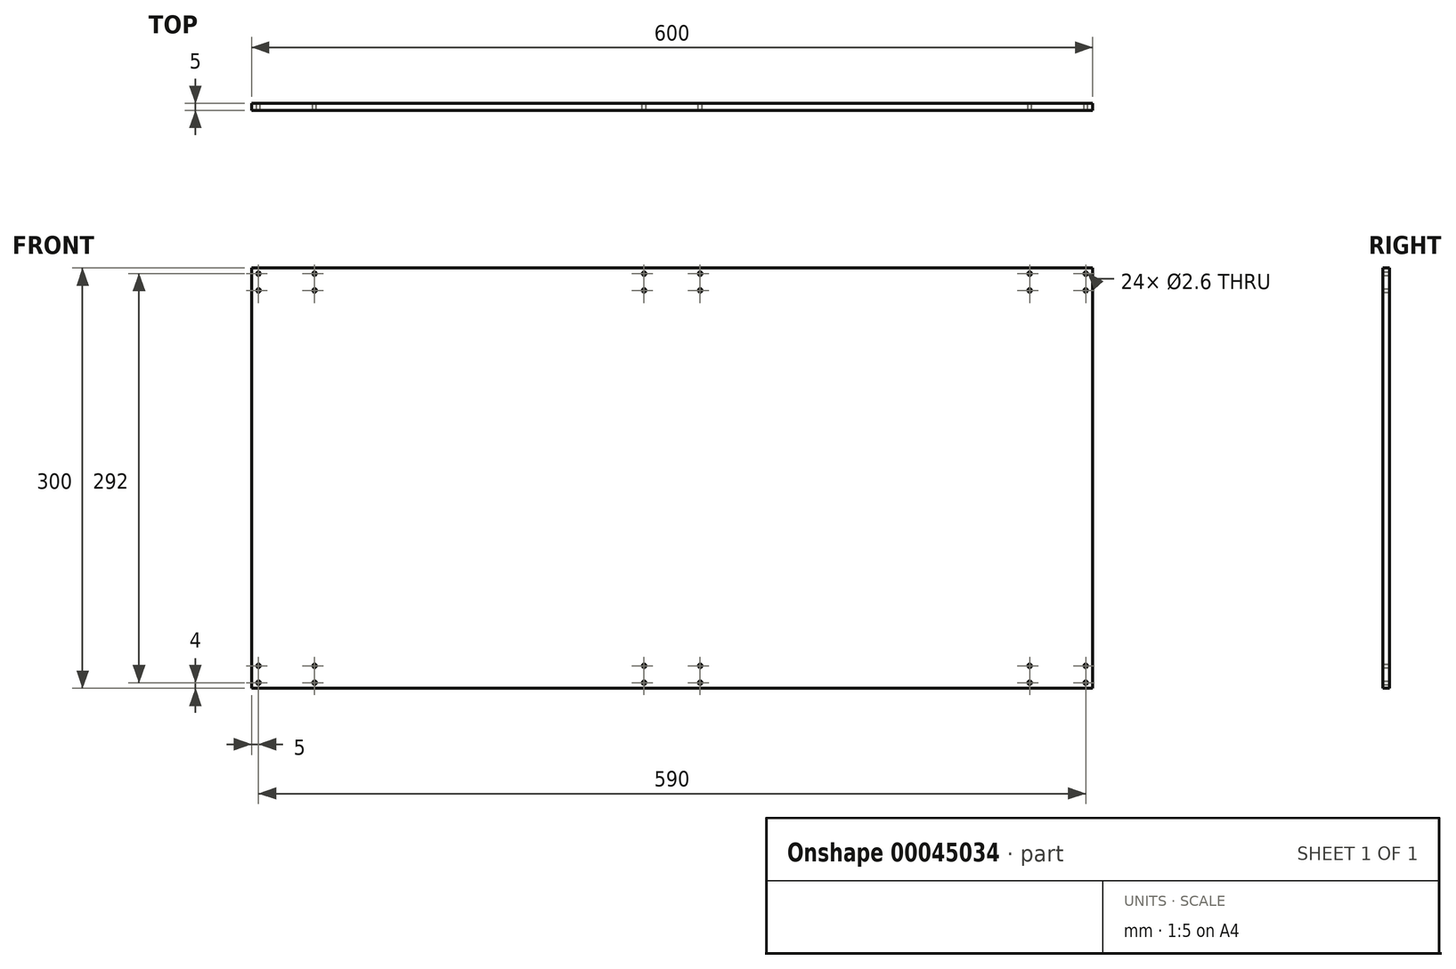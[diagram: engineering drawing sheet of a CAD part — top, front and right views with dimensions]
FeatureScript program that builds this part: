
annotation { "Feature Type Name" : "Feature", "Feature Type Description" : "" }
export const myFeature = defineFeature(function(context is Context, id is Id, definition is map)
    precondition{}
    {
        {
            var Q0;
            Q0=qCreatedBy(makeId("Front.planeOp"),FACE);
            var sketch = newSketch(context, id + "F0", { "sketchPlane" : qUnion([Q0])});
            skLineSegment(sketch, "E0.rect.bottom", {"start": v(300, -150) * mm, "end": v(-300, -150) * mm});
            skLineSegment(sketch, "E0.rect.top", {"start": v(300, 150) * mm, "end": v(-300, 150) * mm});
            skLineSegment(sketch, "E0.rect.left", {"start": v(300, -150) * mm, "end": v(300, 150) * mm});
            skLineSegment(sketch, "E0.rect.right", {"start": v(-300, -150) * mm, "end": v(-300, 150) * mm});
            skCircle(sketch, "E1", {"center": v(-295, 146) * mm, "radius": 1.3 * mm});
            skCircle(sketch, "E2", {"center": v(-295, 134) * mm, "radius": 1.3 * mm});
            skCircle(sketch, "E3", {"center": v(-255, 146) * mm, "radius": 1.3 * mm});
            skCircle(sketch, "E4", {"center": v(-255, 134) * mm, "radius": 1.3 * mm});
            skCircle(sketch, "E5.MirrorC", {"center": v(295, 146) * mm, "radius": 1.3 * mm});
            skCircle(sketch, "E6.MirrorC", {"center": v(295, 134) * mm, "radius": 1.3 * mm});
            skCircle(sketch, "E7.MirrorC", {"center": v(255, 146) * mm, "radius": 1.3 * mm});
            skCircle(sketch, "E8.MirrorC", {"center": v(255, 134) * mm, "radius": 1.3 * mm});
            skLineSegment(sketch, "E9.MirrorCS", {"start": v(-300, 150) * mm, "end": v(300, 150) * mm});
            skCircle(sketch, "E10", {"center": v(-20, 146) * mm, "radius": 1.3 * mm});
            skCircle(sketch, "E11", {"center": v(20, 146) * mm, "radius": 1.3 * mm});
            skCircle(sketch, "E12", {"center": v(-20, 134) * mm, "radius": 1.3 * mm});
            skCircle(sketch, "E13", {"center": v(20, 134) * mm, "radius": 1.3 * mm});
            skCircle(sketch, "E14.MirrorC", {"center": v(295, -146) * mm, "radius": 1.3 * mm});
            skCircle(sketch, "E15.MirrorC", {"center": v(-20, -146) * mm, "radius": 1.3 * mm});
            skCircle(sketch, "E16.MirrorC", {"center": v(20, -146) * mm, "radius": 1.3 * mm});
            skCircle(sketch, "E17.MirrorC", {"center": v(-20, -134) * mm, "radius": 1.3 * mm});
            skCircle(sketch, "E18.MirrorC", {"center": v(-255, -146) * mm, "radius": 1.3 * mm});
            skCircle(sketch, "E19.MirrorC", {"center": v(20, -134) * mm, "radius": 1.3 * mm});
            skCircle(sketch, "E20.MirrorC", {"center": v(-255, -134) * mm, "radius": 1.3 * mm});
            skCircle(sketch, "E21.MirrorC", {"center": v(-295, -146) * mm, "radius": 1.3 * mm});
            skCircle(sketch, "E22.MirrorC", {"center": v(-295, -134) * mm, "radius": 1.3 * mm});
            skCircle(sketch, "E23.MirrorC", {"center": v(295, -134) * mm, "radius": 1.3 * mm});
            skCircle(sketch, "E24.MirrorC", {"center": v(255, -146) * mm, "radius": 1.3 * mm});
            skCircle(sketch, "E25.MirrorC", {"center": v(255, -134) * mm, "radius": 1.3 * mm});
            skLineSegment(sketch, "E26.MirrorCS", {"start": v(-300, -150) * mm, "end": v(300, -150) * mm});
            skSolve(sketch);
        }
        {
            var Q0;
            Q0 = qSketchRegion(id + "F0", true);
            extrude(context, id + "F1", {"entities" : qUnion([Q0]), "depth" : 5 * mm});
        }
    });
